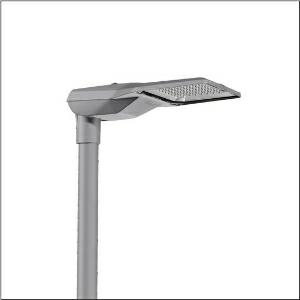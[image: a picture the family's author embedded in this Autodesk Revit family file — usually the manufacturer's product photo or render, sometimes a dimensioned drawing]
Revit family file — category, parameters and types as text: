
# Revit family: streetlight_sl_21_iq_midi___p0_8a_5xe3u31v08mb_d52e
name_source: partatom
category: Lighting Fixtures
units: mm (PartAtom-declared; Revit-internal decimal feet)

## family parameters
Cut with Voids When Loaded = No
Host = Face
Light Source = No
Part Type = Normal
Room Calculation Point = No
Round Connector Dimension = Use Diameter
Shared = No

## types (1)
- --- (1 x LED, 18500 lm, 129.3 W, 3000K)
    Apparent Load = 129 VA
    CIE Flux Codes = 33 69 96 100 100
    Color Rendering = 70
    Color Temperature = 3000K
    Default Elevation = 1800 mm
    Description = Streetlight SL 21 iQ midi, mast luminaire, primary light control with lens, of PMMA, primary optical cover: cover, of toughened safety glass, transparent, light distribution: P0.8a, light emission: direct distribution, primary light characteristic: asymmetric, installation type: post-top, side-entry, LED, High Power LED, rated luminous flux: 18.500lm, luminous efficacy: 143lm/W, light colour: 730, colour temperature: 3000K, control gear: iQ-Street Remote, D4i with power reduction, control: pre-setting: logarithmic dimming characteristic, Street-Remote, Auto-Match, Temp-Guard, Lumen-Switch, Night-Set, Smart-Wire, Light-Fading, Desk-Remote (wireless, voltage-free reading and setting of iQ features in the workshop via application-optimized NFC function/RFID function), optimised constant luminous flux control (CLO 2.0), mains connection: 230..240V, AC, 50/60Hz, start of lifetime: 129W, end of service life: 142W, reduction: 56W, luminaire housing, of diecast aluminium, powder-coated, SITECO metallic grey (DB 702S), corrosivity category C5 high according to DIN EN ISO 12944, please order mast flange separately, inclination adjustable: 0°, 5°, 10°, 15°, sealing non-destructively replaceable, multi-level sealing system, length: 644mm, width: 335mm, height: 110mm, mast flange for spigot size: 42mm (side-entry): 5XC10008XM4, 60/48mm (side-entry/post-top): 5XC10108XM2, 76/60mm (side-entry/post-top): 5XC10108XM1, mounting height: 4..8m, Smart Interface above, protection rating (complete): IP66, insulation class (complete): insulation class II (safety insulation), certification: CE, ENEC, ENEC+, VDE, impact resistance: IK10, permissible operating ambient temperature for outdoor applications: -40..+50°C, standard-compliant lighting for roads and squares, packaging unit: 1 piece

Light Distribution: P0.8a
    Height = 111 mm
    Lamp = 1 x LED
    Lamp Light Flux = 18500 lm
    Lamp Power = 129.3 W
    Lamp count = 1
    Length = 644 mm
    Luminous efficacy = 143 lm/W
    Manufacturer = Siteco
    ModVariant = No
    Model = 5XE3U31V08MB
    Number of Poles = 1
    OnlyDefault = Yes
    Power Factor = 1
    Product Name = Streetlight SL 21 iQ midi | P0.8a
    Product group = mast luminaire | pylon top
    ProductGroupID = 6100
    Protection Class = Protection class II
    Protection Degree = IP 66
    RLX_Detail_Level = 1
    RLX_Emergency_Light_Flux = 0 lm
    RLX_Emergency_Type = 0
    RLX_Emergency_Type_DB = No
    RlxData = <blob elided: 90521 chars, md5=7eedc432>
    Socket = socket
    Standby Power = 0 W
    System Light Flux = 18500 lm
    System Power = 129 W
    Type Comments = factory setting: luminous flux: 100 % | dim-lin: 254 | 672 mA
    Type Image = l_1004302.jpg
    URL = http://relux.com
    VarID = @adj_081687
    Voltage = 0 V
    Weight = 0.00 kg
    Width = 336 mm

## geometry (parser evidence)
native form markers: Blend x4, Sweep x9
no freeform markers — native parametric forms only
